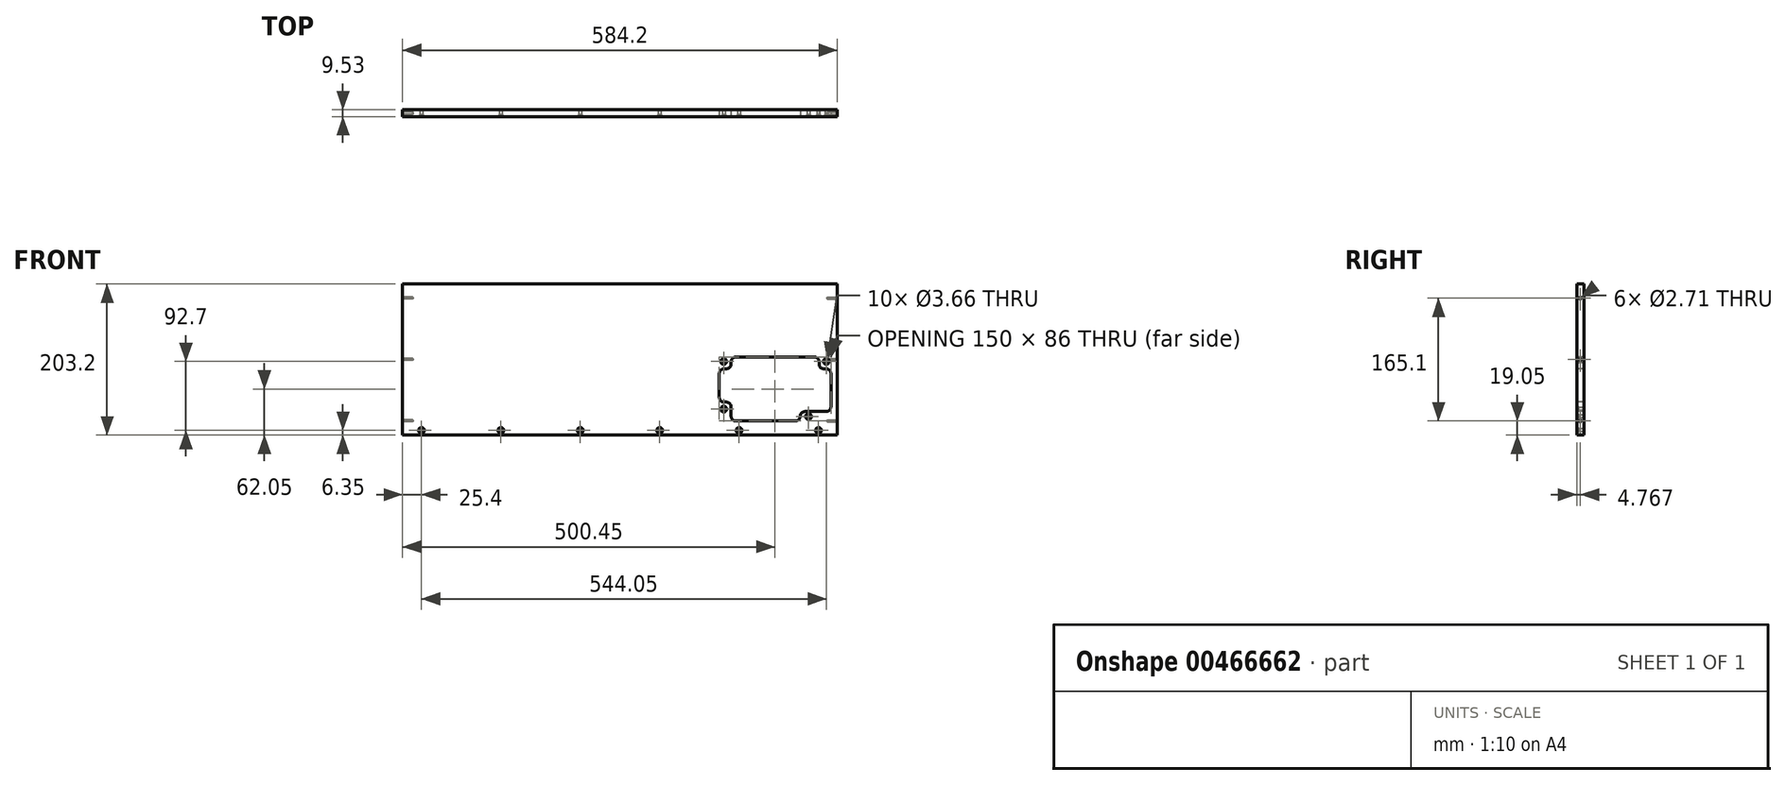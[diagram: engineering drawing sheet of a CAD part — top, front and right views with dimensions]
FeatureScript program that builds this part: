
annotation { "Feature Type Name" : "Feature", "Feature Type Description" : "" }
export const myFeature = defineFeature(function(context is Context, id is Id, definition is map)
    precondition{}
    {
        {
            var Q0;
            Q0=qCreatedBy(makeId("Front.planeOp"),FACE);
            var sketch = newSketch(context, id + "F0", { "sketchPlane" : qUnion([Q0])});
            skLineSegment(sketch, "E0.bottom", {"start": v(0, 0) * mm, "end": v(-584.2, 0) * mm});
            skLineSegment(sketch, "E0.top", {"start": v(0, 203.2) * mm, "end": v(-584.2, 203.2) * mm});
            skLineSegment(sketch, "E0.left", {"start": v(0, 0) * mm, "end": v(0, 203.2) * mm});
            skLineSegment(sketch, "E0.right", {"start": v(-584.2, 0) * mm, "end": v(-584.2, 203.2) * mm});
            skSolve(sketch);
        }
        {
            var Q0;
            Q0 = qSketchRegion(id + "F0", true);
            extrude(context, id + "F1", {"entities" : qUnion([Q0]), "depth" : 9.52 * mm});
        }
        {
            var Q0;
            Q0=makeQuery(id+"F1.opExtrude","CAP_FACE",FACE,{"disambiguationData":[OSD([sQuery(id+"F0.wireOp",EDGE,"E0.bottom"),sQuery(id+"F0.wireOp",EDGE,"E0.top"),sQuery(id+"F0.wireOp",EDGE,"E0.left"),sQuery(id+"F0.wireOp",EDGE,"E0.right")])],"isStart":false});
            var sketch = newSketch(context, id + "F2", { "sketchPlane" : qUnion([Q0])});
            skPoint(sketch, "E1", {"position": v(-25.4, 6.35) * mm});
            skPoint(sketch, "E2.1.0.0", {"position": v(-132.08, 6.35) * mm});
            skPoint(sketch, "E2.2.0.0", {"position": v(-238.76, 6.35) * mm});
            skPoint(sketch, "E2.3.0.0", {"position": v(-345.44, 6.35) * mm});
            skPoint(sketch, "E2.4.0.0", {"position": v(-452.12, 6.35) * mm});
            skPoint(sketch, "E2.5.0.0", {"position": v(-558.8, 6.35) * mm});
            skLineSegment(sketch, "E2.direction1", {"start": v(-25.4, 6.35) * mm, "end": v(-132.08, 6.35) * mm, "construction": true});
            skPoint(sketch, "E3", {"position": v(-152.75, 35.05) * mm});
            skPoint(sketch, "E4", {"position": v(-152.75, 99.05) * mm});
            skPoint(sketch, "E5", {"position": v(-14.75, 99.05) * mm});
            skPoint(sketch, "E6", {"position": v(-38.75, 25.05) * mm});
            skPoint(sketch, "E7", {"position": v(-158.75, 19.05) * mm});
            skLineSegment(sketch, "E8", {"start": v(-158.75, 50.8) * mm, "end": v(-158.75, 82.83) * mm, "construction": true});
            skLineSegment(sketch, "E9", {"start": v(-136.52, 105.05) * mm, "end": v(-30.97, 105.05) * mm, "construction": true});
            skLineSegment(sketch, "E10", {"start": v(-8.75, 82.83) * mm, "end": v(-8.75, 38.1) * mm, "construction": true});
            skLineSegment(sketch, "E11", {"start": v(-56.37, 19.05) * mm, "end": v(-136.52, 19.05) * mm, "construction": true});
            skLineSegment(sketch, "E12.bottom", {"start": v(-136.52, 105.05) * mm, "end": v(-30.97, 105.05) * mm});
            skLineSegment(sketch, "E12.top", {"start": v(-158.75, 19.05) * mm, "end": v(-142.87, 19.05) * mm});
            skLineSegment(sketch, "E12.left", {"start": v(-158.75, 82.83) * mm, "end": v(-158.75, 50.8) * mm});
            skLineSegment(sketch, "E12.right", {"start": v(-8.75, 82.83) * mm, "end": v(-8.75, 38.1) * mm});
            skLineSegment(sketch, "E13", {"start": v(-142.87, 98.7) * mm, "end": v(-142.87, 95.53) * mm});
            skLineSegment(sketch, "E14", {"start": v(-149.22, 89.18) * mm, "end": v(-152.4, 89.18) * mm});
            skLineSegment(sketch, "E15", {"start": v(-15.1, 31.75) * mm, "end": v(-43.67, 31.75) * mm});
            skLineSegment(sketch, "E16", {"start": v(-50.02, 25.4) * mm, "end": v(-50.02, 25.4) * mm});
            skLineSegment(sketch, "E17", {"start": v(-152.4, 44.45) * mm, "end": v(-149.22, 44.45) * mm});
            skLineSegment(sketch, "E18", {"start": v(-142.87, 38.1) * mm, "end": v(-142.87, 25.4) * mm});
            skLineSegment(sketch, "E19", {"start": v(-24.62, 98.7) * mm, "end": v(-24.62, 95.53) * mm});
            skLineSegment(sketch, "E20", {"start": v(-18.27, 89.18) * mm, "end": v(-15.1, 89.18) * mm});
            skPoint(sketch, "E21.newPointA", {"position": v(-158.75, 105.05) * mm});
            skPoint(sketch, "E21.newPointB", {"position": v(-142.87, 105.05) * mm});
            skArc(sketch, "E21.filletArc", {"start": v(-136.52, 105.05) * mm, "mid": v(-141.02, 103.2) * mm, "end": v(-142.87, 98.7) * mm});
            skPoint(sketch, "E22.newPointA", {"position": v(-158.75, 89.18) * mm});
            skArc(sketch, "E22.filletArc", {"start": v(-152.4, 89.18) * mm, "mid": v(-156.9, 87.32) * mm, "end": v(-158.75, 82.83) * mm});
            skPoint(sketch, "E23.newPointA", {"position": v(-158.75, 44.45) * mm});
            skArc(sketch, "E23.filletArc", {"start": v(-158.75, 50.8) * mm, "mid": v(-156.9, 46.3) * mm, "end": v(-152.4, 44.45) * mm});
            skPoint(sketch, "E24.newPointA", {"position": v(-142.87, 19.05) * mm});
            skArc(sketch, "E24.filletArc", {"start": v(-142.87, 25.4) * mm, "mid": v(-141.02, 20.9) * mm, "end": v(-136.52, 19.05) * mm});
            skPoint(sketch, "E25.visualSharp", {"position": v(-142.87, 44.45) * mm});
            skArc(sketch, "E25.filletArc", {"start": v(-142.87, 38.1) * mm, "mid": v(-144.73, 42.6) * mm, "end": v(-149.22, 44.45) * mm});
            skPoint(sketch, "E26.newPointA", {"position": v(-50.02, 19.05) * mm});
            skArc(sketch, "E26.filletArc", {"start": v(-56.37, 19.05) * mm, "mid": v(-51.88, 20.9) * mm, "end": v(-50.02, 25.4) * mm});
            skPoint(sketch, "E27.visualSharp", {"position": v(-50.02, 31.75) * mm});
            skArc(sketch, "E27.filletArc", {"start": v(-43.67, 31.75) * mm, "mid": v(-48.17, 29.9) * mm, "end": v(-50.02, 25.4) * mm});
            skPoint(sketch, "E28.newPointA", {"position": v(-8.75, 31.75) * mm});
            skPoint(sketch, "E28.newPointB", {"position": v(-8.75, 19.05) * mm});
            skArc(sketch, "E28.filletArc", {"start": v(-15.1, 31.75) * mm, "mid": v(-10.6, 33.6) * mm, "end": v(-8.75, 38.1) * mm});
            skPoint(sketch, "E29.newPointA", {"position": v(-8.75, 89.18) * mm});
            skArc(sketch, "E29.filletArc", {"start": v(-8.75, 82.83) * mm, "mid": v(-10.6, 87.32) * mm, "end": v(-15.1, 89.18) * mm});
            skPoint(sketch, "E30.visualSharp", {"position": v(-24.62, 89.18) * mm});
            skArc(sketch, "E30.filletArc", {"start": v(-24.62, 95.53) * mm, "mid": v(-22.77, 91.03) * mm, "end": v(-18.27, 89.18) * mm});
            skPoint(sketch, "E31.newPointA", {"position": v(-24.62, 105.05) * mm});
            skPoint(sketch, "E31.newPointB", {"position": v(-8.75, 105.05) * mm});
            skArc(sketch, "E31.filletArc", {"start": v(-24.62, 98.7) * mm, "mid": v(-26.48, 103.2) * mm, "end": v(-30.97, 105.05) * mm});
            skPoint(sketch, "E32.visualSharp", {"position": v(-142.87, 89.18) * mm});
            skArc(sketch, "E32.filletArc", {"start": v(-149.22, 89.18) * mm, "mid": v(-144.73, 91.03) * mm, "end": v(-142.87, 95.53) * mm});
            skLineSegment(sketch, "E33.trimOffspring", {"start": v(-136.52, 19.05) * mm, "end": v(-56.37, 19.05) * mm});
            skSolve(sketch);
        }
        {
            var Q0;
            Q0=sQuery(id+"F2.wireOp",VERTEX,"3cbaf860-a3b3-4acd-8c4c-f72187c6f7f3.0.2.0");
            var Q1;
            Q1=sQuery(id+"F2.wireOp",VERTEX,"87747e4b-697a-481e-92c6-ee838948ff75.0.1.0");
            var Q2;
            Q2=sQuery(id+"F2.wireOp",VERTEX,"E2.2.0.0");
            var Q3;
            Q3=sQuery(id+"F2.wireOp",VERTEX,"3cbaf860-a3b3-4acd-8c4c-f72187c6f7f3.0.1.0");
            var Q4;
            Q4=sQuery(id+"F2.wireOp",VERTEX,"b1ce3b2f-73ae-466a-80bd-04fea388af39");
            var Q5;
            Q5=sQuery(id+"F2.wireOp",VERTEX,"8f645f1f-6cc1-4812-9c87-8ebc2eae2ba4");
            var Q6;
            Q6=sQuery(id+"F2.wireOp",VERTEX,"E1");
            var Q7;
            Q7=sQuery(id+"F2.wireOp",VERTEX,"E2.3.0.0");
            var Q8;
            Q8=sQuery(id+"F2.wireOp",VERTEX,"87747e4b-697a-481e-92c6-ee838948ff75.0.2.0");
            var Q9;
            Q9=sQuery(id+"F2.wireOp",VERTEX,"E2.5.0.0");
            var Q10;
            Q10=sQuery(id+"F2.wireOp",VERTEX,"E2.1.0.0");
            var Q11;
            Q11=sQuery(id+"F2.wireOp",VERTEX,"E2.4.0.0");
            var Q12;
            Q12=sQuery(id+"F2.wireOp",VERTEX,"E4");
            var Q13;
            Q13=sQuery(id+"F2.wireOp",VERTEX,"E3");
            var Q14;
            Q14=sQuery(id+"F2.wireOp",VERTEX,"E6");
            var Q15;
            Q15=sQuery(id+"F2.wireOp",VERTEX,"E5");
            var Q16;
            Q16=makeQuery(id+"F1.opExtrude","SWEPT_BODY",BODY,{"disambiguationData":[OSD([sQuery(id+"F0.wireOp",EDGE,"E0.bottom"),sQuery(id+"F0.wireOp",EDGE,"E0.top"),sQuery(id+"F0.wireOp",EDGE,"E0.left"),sQuery(id+"F0.wireOp",EDGE,"E0.right")])]});
            hole(context, id + "F3", {"style" : HoleStyle.C_SINK, "endStyle" : HoleEndStyle.BLIND, "standardTappedOrClearance" : lookupTablePath({ "standard" : "ANSI", "fit" : "Close", "size" : "#6", "type" : "Clearance" }), "standardBlindInLast" : lookupTablePath({ "fit" : "Close", "standard" : "ANSI", "size" : "#6", "type" : "Clearance" }), "holeDiameter" : 3.66 * mm, "cSinkDiameter" : 7.8 * mm, "cSinkAngle" : 82 * degree, "holeDepth" : 10.3 * mm, "isTappedThrough" : true, "tappedDepth" : 6.34 * mm, "tapClearance" : 5, "locations" : qUnion([Q0, Q1, Q2, Q3, Q4, Q5, Q6, Q7, Q8, Q9, Q10, Q11, Q12, Q13, Q14, Q15]), "scope" : qUnion([Q16])});
        }
        {
            var Q0;
            Q0=makeQuery(id+"F1.opExtrude","CAP_FACE",FACE,{"disambiguationData":[OSD([sQuery(id+"F0.wireOp",EDGE,"E0.bottom"),sQuery(id+"F0.wireOp",EDGE,"E0.top"),sQuery(id+"F0.wireOp",EDGE,"E0.left"),sQuery(id+"F0.wireOp",EDGE,"E0.right")])],"isStart":false});
            var sketch = newSketch(context, id + "F4", { "sketchPlane" : qUnion([Q0])});
            skLineSegment(sketch, "E34.bottom", {"start": v(-127, 101.6) * mm, "end": v(-25.4, 101.6) * mm});
            skLineSegment(sketch, "E34.top", {"start": v(-127, 31.75) * mm, "end": v(-25.4, 31.75) * mm});
            skLineSegment(sketch, "E34.left", {"start": v(-127, 101.6) * mm, "end": v(-127, 31.75) * mm});
            skLineSegment(sketch, "E34.right", {"start": v(-25.4, 101.6) * mm, "end": v(-25.4, 31.75) * mm});
            skSolve(sketch);
        }
        {
            var Q0;
            Q0 = qSketchRegion(id + "F4", true);
            extrude(context, id + "F5", {"entities" : qUnion([Q0]), "operationType" : NewBodyOperationType.REMOVE, "endBound" : BoundingType.THROUGH_ALL, "oppositeDirection" : true, "depth" : 25.4 * mm});
        }
        {
            var Q0;
            Q0 = qSketchRegion(id + "F2", true);
            extrude(context, id + "F6", {"entities" : qUnion([Q0]), "operationType" : NewBodyOperationType.REMOVE, "oppositeDirection" : true, "depth" : 25.4 * mm});
        }
        {
            var Q0;
            Q0=makeQuery(id+"F1.opExtrude","SWEPT_FACE",FACE,{"disambiguationData":[OSD([sQuery(id+"F0.wireOp",EDGE,"E0.right")])]});
            var sketch = newSketch(context, id + "F7", { "sketchPlane" : qUnion([Q0])});
            skPoint(sketch, "E35", {"position": v(4.76, 19.05) * mm});
            skPoint(sketch, "E36.0.1.0", {"position": v(4.76, 101.6) * mm});
            skPoint(sketch, "E36.0.2.0", {"position": v(4.76, 184.15) * mm});
            skLineSegment(sketch, "E36.direction1", {"start": v(4.76, 19.05) * mm, "end": v(30.16, 19.05) * mm, "construction": true});
            skLineSegment(sketch, "E36.direction2", {"start": v(4.76, 19.05) * mm, "end": v(4.76, 101.6) * mm, "construction": true});
            skSolve(sketch);
        }
        {
            var Q0;
            Q0=makeQuery(id+"F1.opExtrude","SWEPT_FACE",FACE,{"disambiguationData":[OSD([sQuery(id+"F0.wireOp",EDGE,"E0.left")])]});
            var sketch = newSketch(context, id + "F8", { "sketchPlane" : qUnion([Q0])});
            skPoint(sketch, "E37", {"position": v(-4.76, 19.05) * mm});
            skPoint(sketch, "E37.positionSnap0", {"position": v(-4.76, 0) * mm});
            skPoint(sketch, "E38.0.1.0", {"position": v(-4.76, 101.6) * mm});
            skPoint(sketch, "E38.0.2.0", {"position": v(-4.76, 184.15) * mm});
            skLineSegment(sketch, "E38.direction1", {"start": v(-4.76, 19.05) * mm, "end": v(20.64, 19.05) * mm, "construction": true});
            skLineSegment(sketch, "E38.direction2", {"start": v(-4.76, 19.05) * mm, "end": v(-4.76, 101.6) * mm, "construction": true});
            skSolve(sketch);
        }
        {
            var Q0;
            Q0=sQuery(id+"F8.wireOp",VERTEX,"E38.0.2.0");
            var Q1;
            Q1=sQuery(id+"F8.wireOp",VERTEX,"E38.0.1.0");
            var Q2;
            Q2=sQuery(id+"F8.wireOp",VERTEX,"E37");
            var Q3;
            Q3=sQuery(id+"F7.wireOp",VERTEX,"E36.0.2.0");
            var Q4;
            Q4=sQuery(id+"F7.wireOp",VERTEX,"E36.0.1.0");
            var Q5;
            Q5=sQuery(id+"F7.wireOp",VERTEX,"E35");
            var Q6;
            Q6=makeQuery(id+"F1.opExtrude","SWEPT_BODY",BODY,{"disambiguationData":[OSD([sQuery(id+"F0.wireOp",EDGE,"E0.bottom"),sQuery(id+"F0.wireOp",EDGE,"E0.top"),sQuery(id+"F0.wireOp",EDGE,"E0.left"),sQuery(id+"F0.wireOp",EDGE,"E0.right")])]});
            hole(context, id + "F9", {"style" : HoleStyle.SIMPLE, "endStyle" : HoleEndStyle.BLIND, "standardTappedOrClearance" : lookupTablePath({ "standard" : "ANSI", "engagement" : "75%", "pitch" : "32 tpi", "size" : "#6", "type" : "Tapped" }), "standardBlindInLast" : lookupTablePath({ "standard" : "ANSI", "engagement" : "75%", "pitch" : "32 tpi", "size" : "#6", "type" : "Tapped" }), "holeDiameter" : 2.7 * mm, "showTappedDepth" : true, "holeDepth" : 13.5 * mm, "isTappedThrough" : true, "tappedDepth" : 9.52 * mm, "tapClearance" : 5, "locations" : qUnion([Q0, Q1, Q2, Q3, Q4, Q5]), "scope" : qUnion([Q6]), "majorDiameter" : 3.5 * mm});
        }
    });
